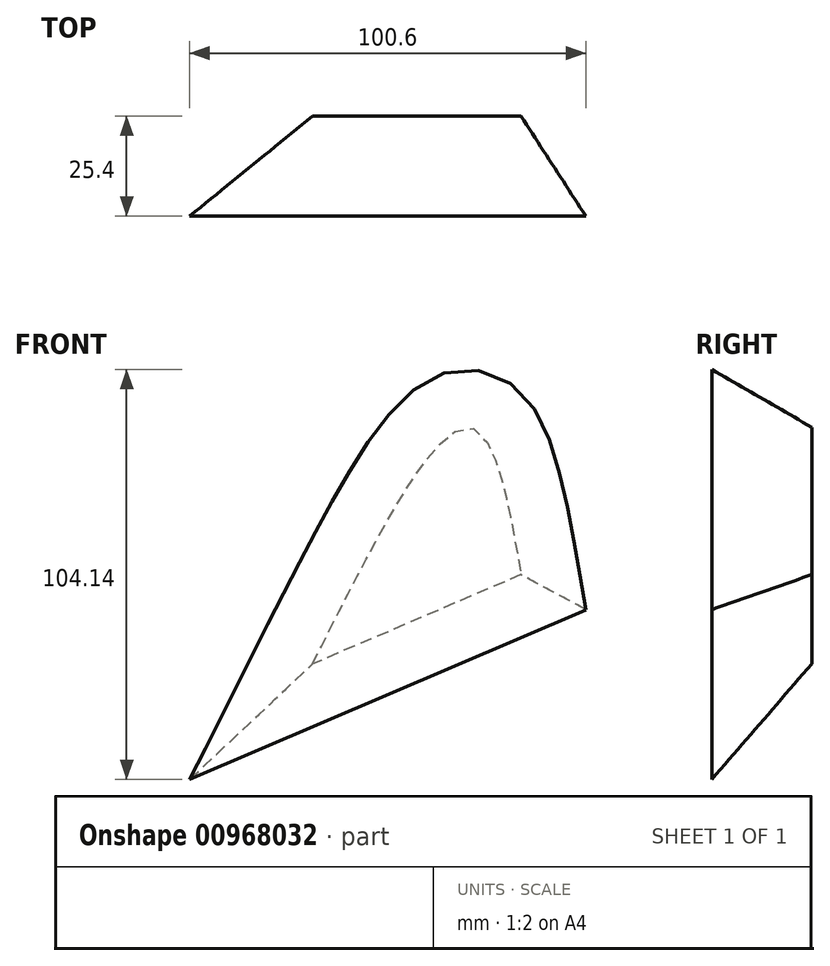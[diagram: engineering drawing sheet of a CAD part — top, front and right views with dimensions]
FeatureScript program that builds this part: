
annotation { "Feature Type Name" : "Feature", "Feature Type Description" : "" }
export const myFeature = defineFeature(function(context is Context, id is Id, definition is map)
    precondition{}
    {
        {
            var Q0;
            Q0=qCreatedBy(makeId("Front.planeOp"),FACE);
            var sketch = newSketch(context, id + "F0", { "sketchPlane" : qUnion([Q0])});
            skFitSpline(sketch, "E0", {"points": [v(-139.7, -22.71) * mm, v(-99.82, 37.41) * mm, v(-86.71, 0) * mm], "startDerivative": vector(80.53, 160) * mm, "endDerivative": vector(22.57, -128.88) * mm});
            skLineSegment(sketch, "E1", {"start": v(-139.7, -22.71) * mm, "end": v(-86.71, 0) * mm});
            skSolve(sketch);
        }
        {
            var Q0;
            Q0=makeQuery(id+"F0.imprint","IMPRINT",FACE,{"disambiguationData":[TD([[makeQuery(id+"F0.imprint","IMPRINT",EDGE,{"derivedFrom":sQuery(id+"F0.wireOp",EDGE,"E0")}),-1.0]])]});
            extrude(context, id + "F1", {"entities" : qUnion([Q0]), "depth" : 25.4 * mm, "offsetDistance" : 25.4 * mm, "hasDraft" : true, "draftAngle" : 30 * degree});
        }
    });
